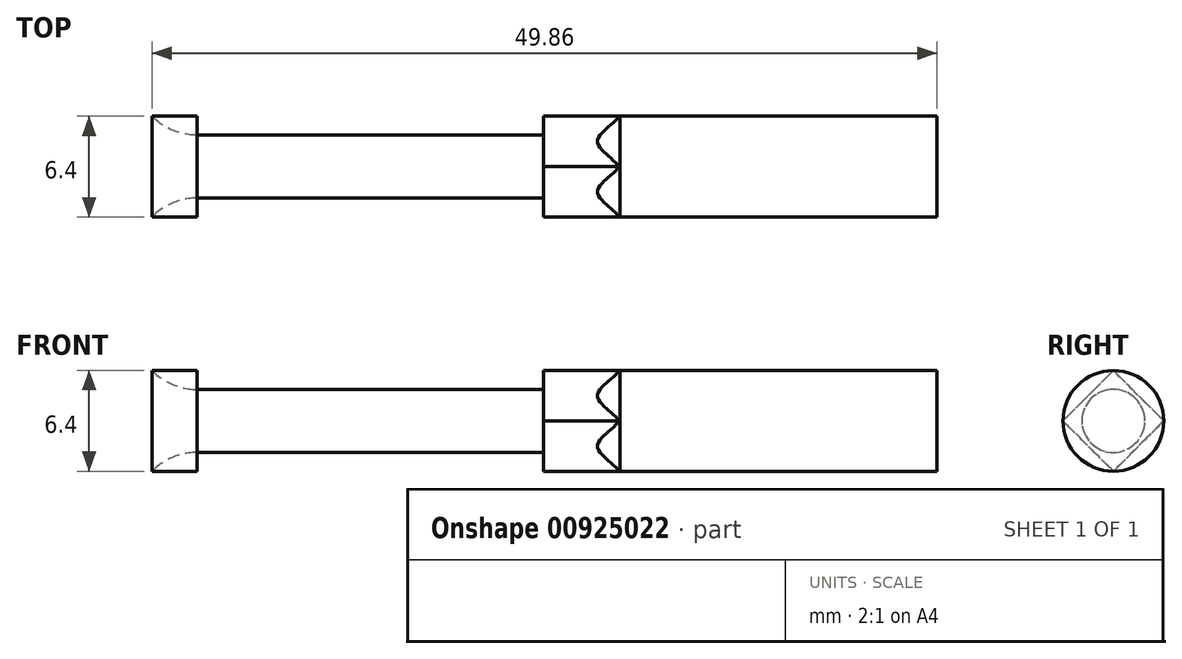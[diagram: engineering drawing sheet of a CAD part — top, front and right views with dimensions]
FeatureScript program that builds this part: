
annotation { "Feature Type Name" : "Feature", "Feature Type Description" : "" }
export const myFeature = defineFeature(function(context is Context, id is Id, definition is map)
    precondition{}
    {
        {
            var Q0;
            Q0=qCreatedBy(makeId("Top.planeOp"),FACE);
            var sketch = newSketch(context, id + "F0", { "sketchPlane" : qUnion([Q0])});
            skLineSegment(sketch, "E0.bottom", {"start": v(-35, 3.2) * mm, "end": v(35, 3.2) * mm});
            skLineSegment(sketch, "E0.top", {"start": v(-35, -3.2) * mm, "end": v(35, -3.2) * mm});
            skLineSegment(sketch, "E0.left", {"start": v(-35, 3.2) * mm, "end": v(-35, -3.2) * mm});
            skLineSegment(sketch, "E0.right", {"start": v(35, 3.2) * mm, "end": v(35, -3.2) * mm});
            skPoint(sketch, "E0.middle", {"position": v(0, 0) * mm});
            skLineSegment(sketch, "E1.bottom", {"start": v(-12, 2) * mm, "end": v(12, 2) * mm});
            skLineSegment(sketch, "E1.top", {"start": v(-12, -2) * mm, "end": v(12, -2) * mm});
            skLineSegment(sketch, "E1.left", {"start": v(-12, 2) * mm, "end": v(-12, -2) * mm});
            skLineSegment(sketch, "E1.right", {"start": v(12, 2) * mm, "end": v(12, -2) * mm});
            skLineSegment(sketch, "E2", {"start": v(12, 2) * mm, "end": v(12, 6) * mm});
            skLineSegment(sketch, "E3", {"start": v(-12, 2) * mm, "end": v(-12, 6) * mm});
            skLineSegment(sketch, "E4", {"start": v(-35, 0) * mm, "end": v(35, 0) * mm});
            skArc(sketch, "E5", {"start": v(12, 2) * mm, "mid": v(13.55, 2.31) * mm, "end": v(14.86, 3.2) * mm});
            skArc(sketch, "E6", {"start": v(-12, 2) * mm, "mid": v(-13.55, 2.31) * mm, "end": v(-14.86, 3.2) * mm});
            skSolve(sketch);
        }
        {
            var Q0;
            {var subQ5=sQuery(id+"F0.wireOp",EDGE,"E6");Q0=makeQuery(id+"F0.imprint","IMPRINT",FACE,{"disambiguationData":[TD([[makeQuery(id+"F0.imprint","IMPRINT",EDGE,{"derivedFrom":subQ5}),1.0]])]});}
            var Q1;
            {var subQ0=sQuery(id+"F0.wireOp",EDGE,"E1.bottom");Q1=makeQuery(id+"F0.imprint","IMPRINT",FACE,{"disambiguationData":[TD([[makeQuery(id+"F0.imprint","IMPRINT",EDGE,{"derivedFrom":subQ0}),-1.0]])]});}
            var Q2;
            {var subQ7=sQuery(id+"F0.wireOp",EDGE,"E5");Q2=makeQuery(id+"F0.imprint","IMPRINT",FACE,{"disambiguationData":[TD([[makeQuery(id+"F0.imprint","IMPRINT",EDGE,{"derivedFrom":subQ7}),-1.0]])]});}
            var Q3;
            Q3=sQuery(id+"F0.wireOp",EDGE,"E4");
            revolve(context, id + "F1", {"surfaceOperationType" : NewSurfaceOperationType.NEW, "entities" : qUnion([Q0, Q1, Q2]), "axis" : qUnion([Q3]), "revolveType" : RevolveType.FULL});
        }
        {
            var Q0;
            Q0=makeQuery(id+"F1.opRevolve","SWEPT_FACE",FACE,{"disambiguationData":[OSD([sQuery(id+"F0.wireOp",EDGE,"E0.right")])]});
            var sketch = newSketch(context, id + "F2", { "sketchPlane" : qUnion([Q0])});
            skLineSegment(sketch, "E7", {"start": v(3.2, 0) * mm, "end": v(0, 3.2) * mm});
            skLineSegment(sketch, "E8", {"start": v(0, 3.2) * mm, "end": v(-3.2, 0) * mm});
            skLineSegment(sketch, "E9", {"start": v(-3.2, 0) * mm, "end": v(0, -3.2) * mm});
            skLineSegment(sketch, "E10", {"start": v(0, -3.2) * mm, "end": v(3.2, 0) * mm});
            skLineSegment(sketch, "E11.0", {"start": v(4.54, 0) * mm, "end": v(0, 4.54) * mm});
            skLineSegment(sketch, "E11.1", {"start": v(0, -4.54) * mm, "end": v(4.54, 0) * mm});
            skLineSegment(sketch, "E11.2", {"start": v(-4.54, 0) * mm, "end": v(0, -4.54) * mm});
            skLineSegment(sketch, "E11.3", {"start": v(0, 4.54) * mm, "end": v(-4.54, 0) * mm});
            skCircle(sketch, "E12", {"center": v(0, 0) * mm, "radius": 4.54 * mm});
            skSolve(sketch);
        }
        {
            var Q0;
            Q0=makeQuery(id+"F2.imprint","IMPRINT",FACE,{"disambiguationData":[TD([[makeQuery(id+"F2.imprint","IMPRINT",EDGE,{"derivedFrom":sQuery(id+"F2.wireOp",EDGE,"E7")}),1.0]])]});
            extrude(context, id + "F3", {"entities" : qUnion([Q0]), "operationType" : NewBodyOperationType.ADD, "oppositeDirection" : true, "depth" : 25 * mm, "offsetDistance" : 25 * mm});
        }
    });
